annotation { "Feature Type Name" : "Feature", "Feature Type Description" : "" }
export const myFeature = defineFeature(function(context is Context, id is Id, definition is map)
    precondition{}
    {
        {
            var Q0;
            Q0=qCreatedBy(makeId("Front.planeOp"),FACE);
            var sketch = newSketch(context, id + "F0", { "sketchPlane" : qUnion([Q0])});
            skLineSegment(sketch, "E0.bottom", {"start": v(-38.1, 57.15) * mm, "end": v(38.1, 57.15) * mm});
            skLineSegment(sketch, "E0.top", {"start": v(-38.1, -57.15) * mm, "end": v(38.1, -57.15) * mm});
            skLineSegment(sketch, "E0.left", {"start": v(-38.1, 57.15) * mm, "end": v(-38.1, -57.15) * mm});
            skLineSegment(sketch, "E0.right", {"start": v(38.1, 57.15) * mm, "end": v(38.1, -57.15) * mm});
            skPoint(sketch, "E0.middle", {"position": v(0, 0) * mm});
            skSolve(sketch);
        }
        {
            var Q0;
            Q0 = qSketchRegion(id + "F0", true);
            extrude(context, id + "F1", {"entities" : qUnion([Q0]), "depth" : 3.17 * mm});
        }
        {
            var Q0;
            Q0=makeQuery(id+"F1.opExtrude","CAP_FACE",FACE,{"disambiguationData":[OSD([sQuery(id+"F0.wireOp",EDGE,"E0.bottom"),sQuery(id+"F0.wireOp",EDGE,"E0.top"),sQuery(id+"F0.wireOp",EDGE,"E0.left"),sQuery(id+"F0.wireOp",EDGE,"E0.right")])],"isStart":false});
            var sketch = newSketch(context, id + "F2", { "sketchPlane" : qUnion([Q0])});
            skText(sketch, "E1", { "text": "Hall Pass", "fontName": "AllertaStencil-Regular.ttf"});
            const initialGuessF2  = {"E1": [-0.032, 0.03164, 1, 0, 0.01115]};
            skSetInitialGuess(sketch, initialGuessF2);
            skSolve(sketch);
        }
        {
            var Q0;
            Q0 = qSketchRegion(id + "F2", true);
            extrude(context, id + "F3", {"entities" : qUnion([Q0]), "operationType" : NewBodyOperationType.REMOVE, "oppositeDirection" : true, "depth" : 3.17 * mm});
        }
        {
            var Q0;
            {var subQ0=sQuery(id+"F0.wireOp",EDGE,"E0.top");var subQ1=sQuery(id+"F0.wireOp",EDGE,"E0.right");var subQ2=sQuery(id+"F0.wireOp",EDGE,"E0.bottom");var subQ3=sQuery(id+"F0.wireOp",EDGE,"E0.left");Q0=makeQuery(id+"F3.boolean.opBoolean","SPLIT",FACE,{"disambiguationData":[TD([makeQuery(id+"F1.opExtrude","SWEPT_FACE",FACE,{"disambiguationData":[OSD([subQ2])]})])],"derivedFrom":makeQuery(id+"F1.opExtrude","CAP_FACE",FACE,{"disambiguationData":[OSD([subQ2,subQ0,subQ3,subQ1])],"isStart":false})});}
            var sketch = newSketch(context, id + "F4", { "sketchPlane" : qUnion([Q0])});
            skFitSpline(sketch, "E2", {"points": [v(-17.03, 11.58) * mm, v(-7, 6) * mm, v(-6.7, 6.15) * mm, v(-3.04, 12.6) * mm, v(-0.45, 17) * mm, v(0.66, 18.95) * mm, v(2.09, 20.28) * mm, v(4.94, 21.73) * mm, v(4.79, 22.18) * mm, v(1.1, 22.12) * mm, v(-5.02, 22.04) * mm, v(-8.6, 21.93) * mm, v(-9.4, 21.82) * mm, v(-11.14, 20.95) * mm, v(-13.89, 17.26) * mm, v(-16.22, 12.96) * mm, v(-16.78, 12.04) * mm, v(-17.03, 11.58) * mm]});
            skFitSpline(sketch, "E3", {"points": [v(8.06, 20.92) * mm, v(4.9, 20.65) * mm, v(0.98, 17.01) * mm, v(-0.44, 14.91) * mm, v(0, 14.2) * mm, v(2.7, 9.87) * mm, v(3.51, 8.4) * mm, v(1.94, 7.26) * mm, v(0.5, 6.54) * mm, v(3.68, 6.4) * mm, v(11.54, 6.33) * mm, v(11.8, 6.43) * mm, v(13.52, 9.5) * mm, v(15.34, 12.83) * mm, v(16.5, 15.13) * mm, v(16.5, 15.75) * mm, v(15.44, 15.18) * mm, v(13.35, 14.4) * mm, v(13.09, 14.97) * mm, v(11.7, 17) * mm, v(9.6, 20) * mm, v(8.06, 20.92) * mm]});
            skFitSpline(sketch, "E4", {"points": [v(18.31, 6.87) * mm, v(15.02, 4.94) * mm, v(11.04, 2.47) * mm, v(8.54, 0.92) * mm, v(8.75, 0.55) * mm, v(10.9, -2.85) * mm, v(13.42, -6.94) * mm, v(15.72, -10.71) * mm, v(16.9, -13.32) * mm, v(16.96, -15.07) * mm, v(16.77, -17.09) * mm], "startDerivative": vector(-28.67, -16.27) * mm, "endDerivative": vector(-2.55, -24.97) * mm});
            skFitSpline(sketch, "E5", {"points": [v(16.77, -17.09) * mm, v(17.43, -16.16) * mm, v(18.4, -14.55) * mm, v(19.2, -12.98) * mm, v(21.24, -9.8) * mm, v(23, -6.42) * mm, v(23.83, -4.81) * mm, v(23.65, -2.78) * mm, v(22.14, 0.66) * mm, v(20.18, 3.75) * mm, v(18.31, 6.87) * mm], "startDerivative": vector(9.4, 12.82) * mm, "endDerivative": vector(-15.57, 26.9) * mm});
            skPoint(sketch, "E6.8.internal.snap0", {"position": v(0, -57.15) * mm});
            skPoint(sketch, "E6.9.internal.snap0", {"position": v(0, -57.15) * mm});
            skFitSpline(sketch, "E6", {"points": [v(13.18, -9.5) * mm, v(8.11, -9.48) * mm, v(5.53, -9.5) * mm, v(5.48, -9.4) * mm, v(5.48, -8.15) * mm, v(5.38, -6.42) * mm, v(4.38, -7.77) * mm, v(2.39, -11.32) * mm, v(0, -15.39) * mm, v(0, -15.68) * mm, v(1.5, -18.3) * mm, v(4.05, -22.16) * mm, v(5.45, -24.69) * mm, v(5.74, -24.3) * mm, v(6, -20.9) * mm, v(6.1, -20.96) * mm, v(10.45, -20.5) * mm, v(11.17, -20.4) * mm, v(13.89, -19.92) * mm, v(15.13, -18.58) * mm, v(15.6, -17.09) * mm, v(15.83, -15.33) * mm, v(15.44, -13.46) * mm, v(14.28, -11.03) * mm, v(13.18, -9.5) * mm]});
            skFitSpline(sketch, "E7", {"points": [v(-4.15, -9.22) * mm, v(-4.2, -20.4) * mm, v(-4.61, -20.53) * mm, v(-9.48, -20.46) * mm, v(-13.74, -20.48) * mm, v(-16.62, -19.6) * mm, v(-18.62, -16.7) * mm, v(-21.9, -10.5) * mm, v(-23.53, -7.5) * mm, v(-23.39, -7.36) * mm, v(-22, -8.23) * mm, v(-17.59, -9.14) * mm, v(-10.87, -9.07) * mm, v(-6.1, -9.14) * mm, v(-4.84, -9.04) * mm, v(-4.15, -9.22) * mm]});
            skFitSpline(sketch, "E8", {"points": [v(-24.24, 6.87) * mm, v(-15.38, 6.87) * mm, v(-13.75, 6.87) * mm, v(-13.63, 6.87) * mm, v(-12.85, 5.4) * mm, v(-11, 2.02) * mm, v(-9.43, -1.28) * mm, v(-8.6, -2.75) * mm, v(-10.12, -1.81) * mm, v(-11.27, -1.25) * mm, v(-11.64, -1.09) * mm, v(-12.49, -2.84) * mm, v(-14.56, -5.83) * mm, v(-15.49, -7.38) * mm, v(-15.98, -7.75) * mm, v(-19.08, -7.52) * mm, v(-22.59, -6.42) * mm], "startDerivative": vector(80.45, 0.4) * mm, "endDerivative": vector(-37.5, 15.81) * mm});
            skFitSpline(sketch, "E9", {"points": [v(-22.59, -6.42) * mm, v(-24.03, -4.9) * mm, v(-24.84, -3.06) * mm, v(-24.78, -1.53) * mm, v(-23.7, 0.47) * mm, v(-23.03, 1.84) * mm, v(-22.16, 3.35) * mm, v(-21.52, 4.73) * mm, v(-21.87, 4.9) * mm, v(-23.12, 5.77) * mm, v(-24.24, 6.87) * mm], "startDerivative": vector(-13.59, 12.1) * mm, "endDerivative": vector(-10.43, 10.92) * mm});
            skSolve(sketch);
        }
        {
            var Q0;
            Q0 = qSketchRegion(id + "F4", true);
            extrude(context, id + "F5", {"entities" : qUnion([Q0]), "operationType" : NewBodyOperationType.REMOVE, "oppositeDirection" : true, "depth" : 3.17 * mm});
        }
        {
            var Q0;
            {var subQ0=sQuery(id+"F0.wireOp",EDGE,"E0.top");var subQ1=sQuery(id+"F0.wireOp",EDGE,"E0.right");var subQ2=sQuery(id+"F0.wireOp",EDGE,"E0.bottom");var subQ3=sQuery(id+"F0.wireOp",EDGE,"E0.left");Q0=makeQuery(id+"F3.boolean.opBoolean","SPLIT",FACE,{"disambiguationData":[TD([makeQuery(id+"F1.opExtrude","SWEPT_FACE",FACE,{"disambiguationData":[OSD([subQ2])]})])],"derivedFrom":makeQuery(id+"F1.opExtrude","CAP_FACE",FACE,{"disambiguationData":[OSD([subQ2,subQ0,subQ3,subQ1])],"isStart":false})});}
            var sketch = newSketch(context, id + "F6", { "sketchPlane" : qUnion([Q0])});
            skCircle(sketch, "E10", {"center": v(0, 51.24) * mm, "radius": 3.18 * mm});
            skSolve(sketch);
        }
        {
            var Q0;
            Q0=makeQuery(id+"F6.imprint","IMPRINT",FACE,{"disambiguationData":[TD([[makeQuery(id+"F6.imprint","IMPRINT",EDGE,{"derivedFrom":sQuery(id+"F6.wireOp",EDGE,"E10")}),1.0]])]});
            var Q1;
            Q1=sQuery(id+"F6.wireOp",EDGE,"E10");
            extrude(context, id + "F7", {"entities" : qUnion([Q0]), "operationType" : NewBodyOperationType.REMOVE, "surfaceEntities" : qUnion([Q1]), "oppositeDirection" : true, "depth" : 3.17 * mm});
        }
        {
            var Q0;
            Q0=makeQuery(id+"F1.opExtrude","CAP_FACE",FACE,{"disambiguationData":[OSD([sQuery(id+"F0.wireOp",EDGE,"E0.bottom"),sQuery(id+"F0.wireOp",EDGE,"E0.top"),sQuery(id+"F0.wireOp",EDGE,"E0.left"),sQuery(id+"F0.wireOp",EDGE,"E0.right")])],"isStart":false});
            var sketch = newSketch(context, id + "F8", { "sketchPlane" : qUnion([Q0])});
            skText(sketch, "E11", { "text": "S.T.E.M", "fontName": "AllertaStencil-Regular.ttf"});
            const initialGuessF8  = {"E11": [-0.03534, -0.0499, 1, 0, 0.01612]};
            skSetInitialGuess(sketch, initialGuessF8);
            skSolve(sketch);
        }
        {
            var Q0;
            Q0 = qSketchRegion(id + "F8", true);
            extrude(context, id + "F9", {"entities" : qUnion([Q0]), "operationType" : NewBodyOperationType.REMOVE, "oppositeDirection" : true, "depth" : 3.17 * mm});
        }
    });